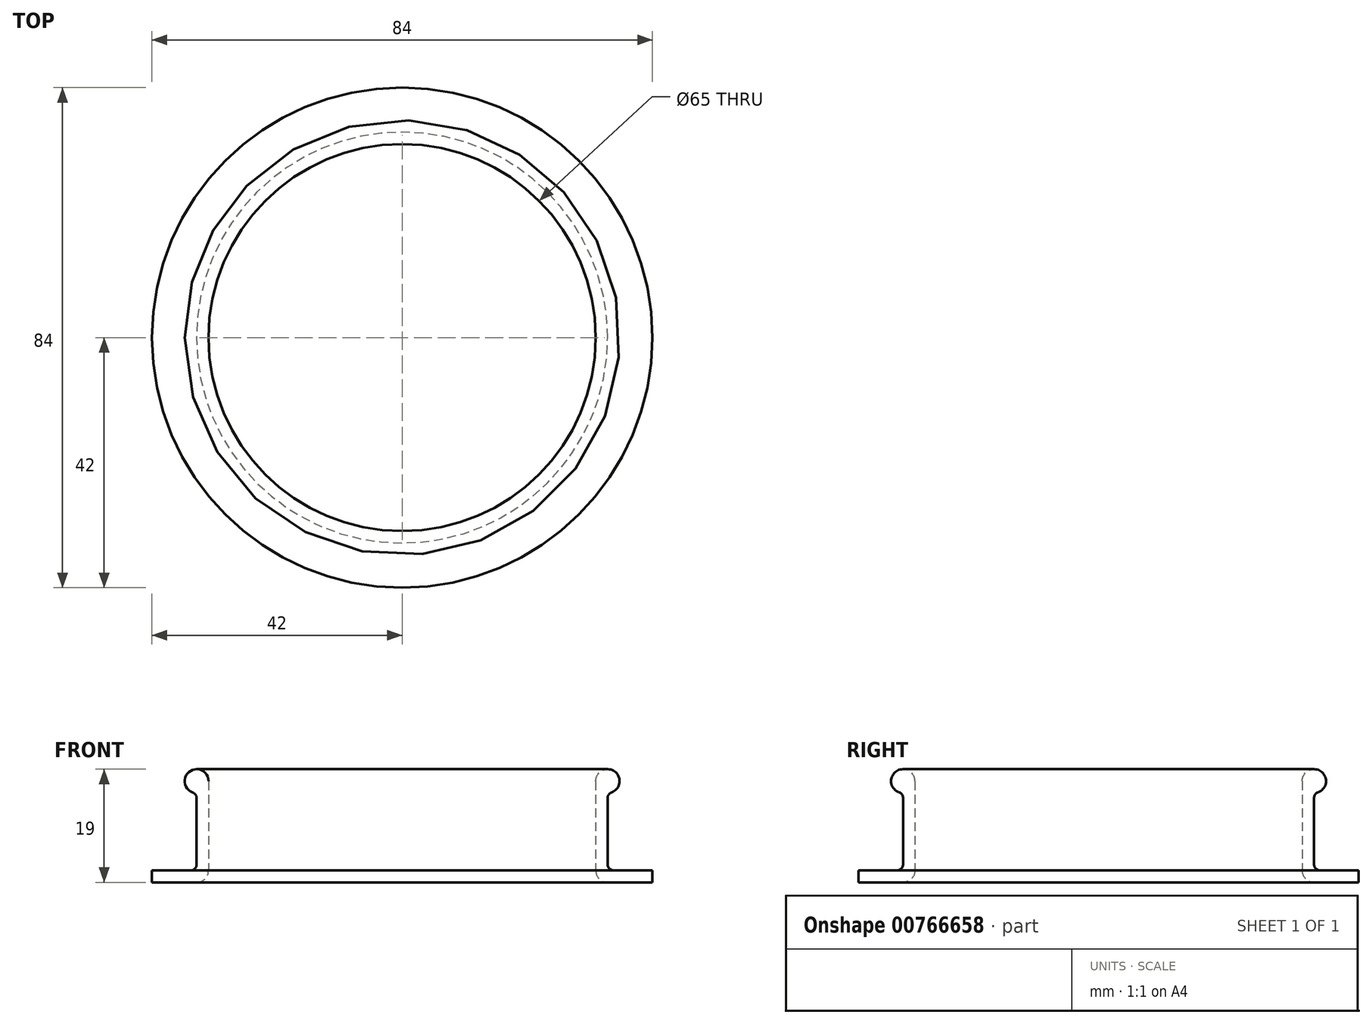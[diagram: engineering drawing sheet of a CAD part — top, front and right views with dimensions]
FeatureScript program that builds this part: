
annotation { "Feature Type Name" : "Feature", "Feature Type Description" : "" }
export const myFeature = defineFeature(function(context is Context, id is Id, definition is map)
    precondition{}
    {
        {
            var Q0;
            Q0=qCreatedBy(makeId("Top.planeOp"),FACE);
            var sketch = newSketch(context, id + "F0", { "sketchPlane" : qUnion([Q0])});
            skCircle(sketch, "E0", {"center": v(0, 0) * mm, "radius": 42 * mm});
            skCircle(sketch, "E1", {"center": v(0, 0) * mm, "radius": 36.5 * mm});
            skSolve(sketch);
        }
        {
            var Q0;
            Q0 = qSketchRegion(id + "F0", true);
            extrude(context, id + "F1", {"entities" : qUnion([Q0]), "depth" : 2 * mm, "offsetDistance" : 25 * mm});
        }
        {
            var Q0;
            Q0=qCreatedBy(makeId("Front.planeOp"),FACE);
            var sketch = newSketch(context, id + "F2", { "sketchPlane" : qUnion([Q0])});
            skLineSegment(sketch, "E2", {"start": v(0, 0) * mm, "end": v(0, 127.1) * mm, "construction": true});
            skLineSegment(sketch, "E3.0", {"start": v(-36.5, 0) * mm, "end": v(0, 0) * mm});
            skLineSegment(sketch, "E4.0", {"start": v(-36.5, 2) * mm, "end": v(0, 2) * mm});
            skLineSegment(sketch, "E5", {"start": v(36.5, 2) * mm, "end": v(36.5, 0) * mm});
            skLineSegment(sketch, "E6", {"start": v(34.5, 3) * mm, "end": v(34.5, 14.17) * mm});
            skLineSegment(sketch, "E7", {"start": v(32.5, 2) * mm, "end": v(32.5, 17) * mm});
            skLineSegment(sketch, "E8.trimOffspring", {"start": v(35.5, 2) * mm, "end": v(36.5, 2) * mm});
            skLineSegment(sketch, "E9.trimOffspring", {"start": v(34.5, 0) * mm, "end": v(36.5, 0) * mm});
            skArc(sketch, "E10", {"start": v(35.17, 15.11) * mm, "mid": v(35.65, 18.63) * mm, "end": v(32.5, 17) * mm});
            skPoint(sketch, "E11.visualSharp", {"position": v(34.5, 2) * mm});
            skArc(sketch, "E11.filletArc", {"start": v(34.5, 3) * mm, "mid": v(34.8, 2.3) * mm, "end": v(35.5, 2) * mm});
            skPoint(sketch, "E12.visualSharp", {"position": v(32.5, 0) * mm});
            skArc(sketch, "E12.filletArc", {"start": v(32.5, 2) * mm, "mid": v(33.09, 0.59) * mm, "end": v(34.5, 0) * mm});
            skPoint(sketch, "E13.visualSharp", {"position": v(34.5, 15) * mm});
            skArc(sketch, "E13.filletArc", {"start": v(35.17, 15.11) * mm, "mid": v(34.68, 14.75) * mm, "end": v(34.5, 14.17) * mm});
            skSolve(sketch);
        }
        {
            var Q0;
            Q0 = qSketchRegion(id + "F2", true);
            var Q1;
            Q1=sQuery(id+"F2.wireOp",EDGE,"E2");
            revolve(context, id + "F3", {"operationType" : NewBodyOperationType.ADD, "surfaceOperationType" : NewSurfaceOperationType.NEW, "entities" : qUnion([Q0]), "axis" : qUnion([Q1]), "revolveType" : RevolveType.FULL});
        }
    });
